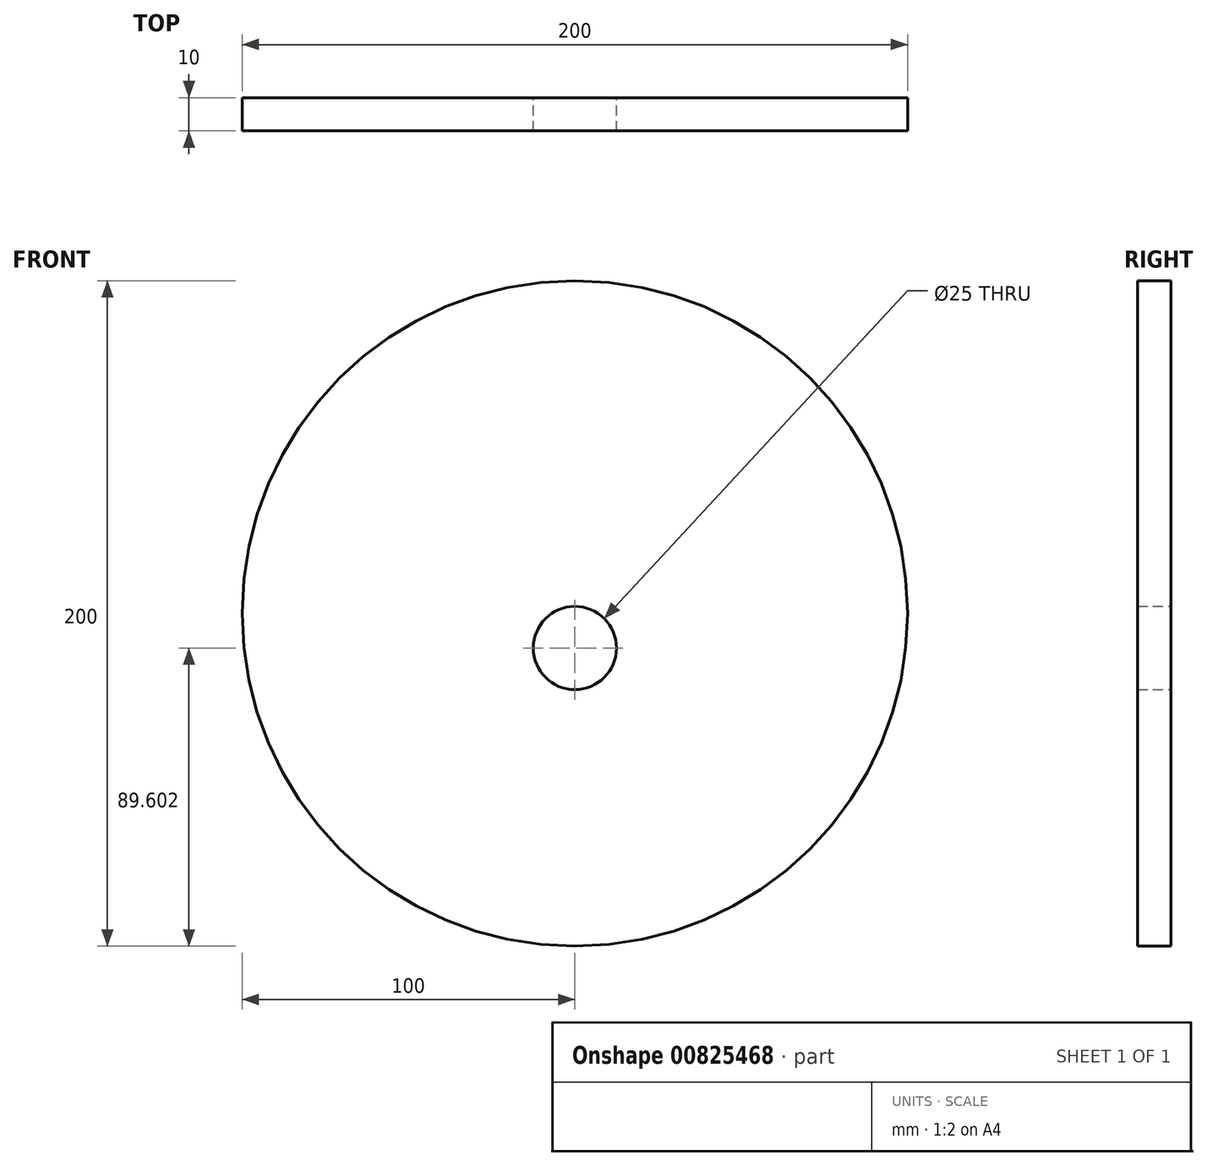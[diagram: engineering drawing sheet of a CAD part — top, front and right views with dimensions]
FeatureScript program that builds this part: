
annotation { "Feature Type Name" : "Feature", "Feature Type Description" : "" }
export const myFeature = defineFeature(function(context is Context, id is Id, definition is map)
    precondition{}
    {
        {
            var Q0;
            Q0=qCreatedBy(makeId("Front.planeOp"),FACE);
            var sketch = newSketch(context, id + "F0", { "sketchPlane" : qUnion([Q0])});
            skCircle(sketch, "E0", {"center": v(0, 0) * mm, "radius": 100 * mm});
            skPoint(sketch, "E1", {"position": v(0, -10.4) * mm});
            skCircle(sketch, "E2", {"center": v(0, -10.4) * mm, "radius": 12.5 * mm});
            skSolve(sketch);
        }
        {
            var Q0;
            Q0=makeQuery(id+"F0.imprint","IMPRINT",FACE,{"disambiguationData":[TD([[makeQuery(id+"F0.imprint","IMPRINT",EDGE,{"derivedFrom":sQuery(id+"F0.wireOp",EDGE,"E0")}),1.0]])]});
            extrude(context, id + "F1", {"entities" : qUnion([Q0]), "depth" : 10 * mm, "offsetDistance" : 25 * mm});
        }
    });
